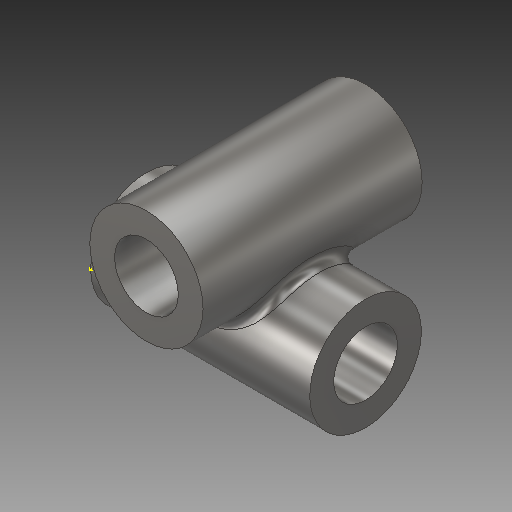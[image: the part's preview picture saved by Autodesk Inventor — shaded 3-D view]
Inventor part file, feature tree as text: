
AUTODESK INVENTOR PART (.ipt)
format: ipt  version: 2018 (Build 220112000, 112)  size: 211,968 bytes
history: native  units: mm
features: sketch x5, extrude x4, plane x1, fillet x1
ambient origin geometry x8: Origin, YZ Plane, XZ Plane, XY Plane, X Axis, Y Axis, Z Axis, Center Point
bodies: Solid1 (feature_tree)
feature tree (11):
  extrude  "Extrusion1"  Depth=32.0mm
  plane  "Work Plane1"
  extrude  "Extrusion2"  Depth=32.0mm
  sketch  "Sketch3"  dims[d7=27.0mm d8=83.0mm d9=0.0mm d10=0.0mm d11=4.0mm]
  fillet  "Fillet1"  Radius=4.0mm
  extrude  "Extrusion3"  Depth=27.0mm TaperAngle=0.0deg
  extrude  "Extrusion4"  [1 undecoded]
  sketch  "Sketch1"  dims[d0=56.0mm d1=32.0mm]
  sketch  "Sketch2"  dims[d2=110.0mm d3=0.0mm d6=32.0mm]
  sketch  "Sketch4"  dims[d12=27.0mm d13=0.0mm d14=27.0mm d15=0.0mm]
  sketch  "Sketch5"
note: 1 required parameter value undecoded (feature->parameter linkage not recoverable at this tier; creation-order binding heuristic only, values carry confidence <= 0.55)
